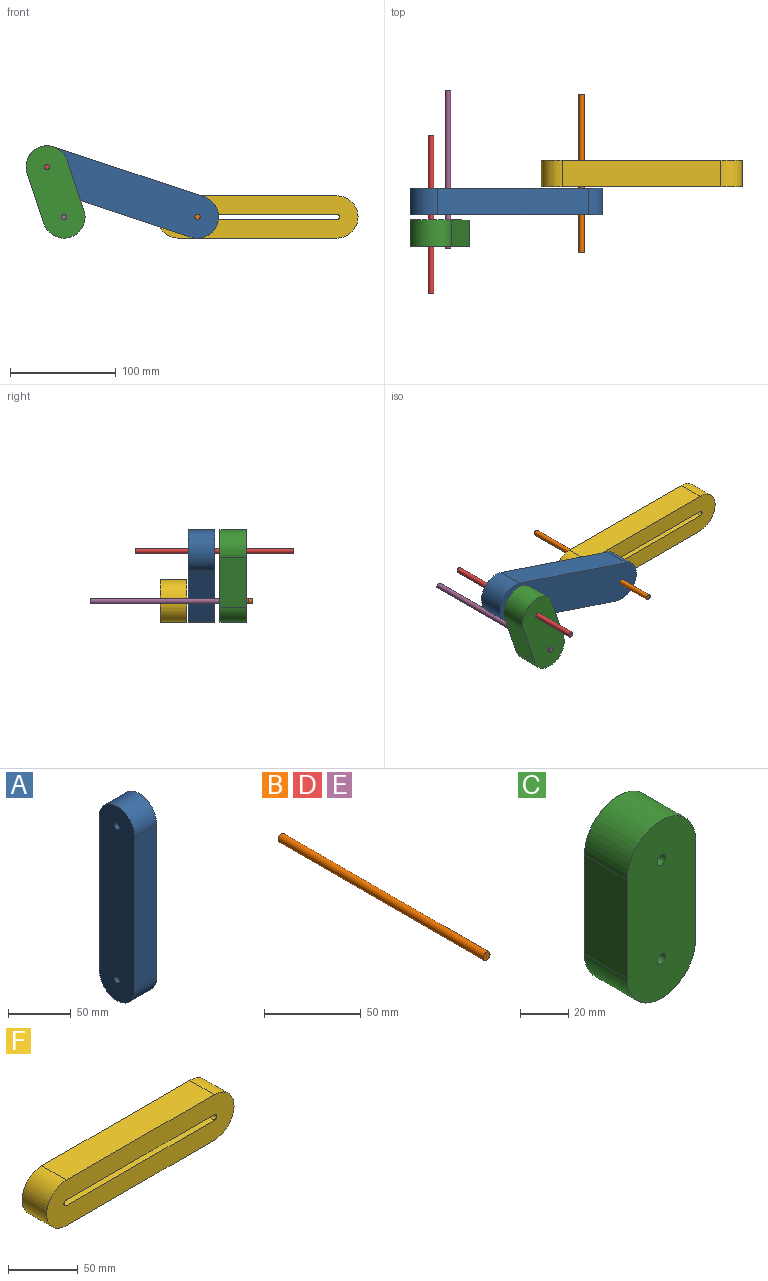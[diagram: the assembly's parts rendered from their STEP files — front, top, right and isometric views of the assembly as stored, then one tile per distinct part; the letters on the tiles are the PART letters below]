
ASSEMBLY  parts=6 mates=5
PART A: 8 faces, bbox 25x40x190 mm
  f0: plane 150x25mm, normal (0,-1,0), area 3750mm2, adj f1,f4,f6,f7
  f1: cylinder r=20mm len=40mm, axis (-1,0,0), area 1570.8mm2, adj f0,f2,f6,f7
  f2: plane 150x25mm, normal (0,1,0), area 3750mm2, adj f1,f4,f6,f7
  f3: cylinder r=2.5mm len=25mm, axis (-1,0,0), area 392.7mm2, adj f6,f7
  f4: cylinder r=20mm len=40mm, axis (-1,0,0), area 1570.8mm2, adj f0,f2,f6,f7
  f5: cylinder r=2.5mm len=25mm, axis (-1,0,0), area 392.7mm2, adj f6,f7
  f6: plane 190x40mm, normal (1,0,0), area 7217.4mm2, adj f0,f1,f2,f3,f4,f5
  f7: plane 190x40mm, normal (-1,0,0), area 7217.4mm2, adj f0,f1,f2,f3,f4,f5
PART B: 3 faces, bbox 5x150x5 mm
  f0: cylinder r=2.5mm len=150mm, axis (0,1,0), area 2356.2mm2, adj f1,f2
  f1: plane 5x5mm, normal (0,-1,0), area 19.6mm2, adj f0
  f2: plane 5x5mm, normal (0,1,0), area 19.6mm2, adj f0
PART C: 8 faces, bbox 40x25x90 mm
  f0: plane 50x25mm, normal (1,0,0), area 1250mm2, adj f1,f4,f6,f7
  f1: cylinder r=20mm len=40mm, axis (0,1,0), area 1570.8mm2, adj f0,f2,f6,f7
  f2: plane 50x25mm, normal (-1,0,0), area 1250mm2, adj f1,f4,f6,f7
  f3: cylinder r=2.5mm len=25mm, axis (0,1,0), area 392.7mm2, adj f6,f7
  f4: cylinder r=20mm len=40mm, axis (0,1,0), area 1570.8mm2, adj f0,f2,f6,f7
  f5: cylinder r=2.5mm len=25mm, axis (0,1,0), area 392.7mm2, adj f6,f7
  f6: plane 90x40mm, normal (0,-1,0), area 3217.4mm2, adj f0,f1,f2,f3,f4,f5
  f7: plane 90x40mm, normal (0,1,0), area 3217.4mm2, adj f0,f1,f2,f3,f4,f5
PART D: same geometry as B
PART E: same geometry as B
PART F: 10 faces, bbox 190x25x40 mm
  f0: plane 150x25mm, normal (0,0,-1), area 3750mm2, adj f1,f7,f8,f9
  f1: cylinder r=2.5mm len=25mm, axis (0,1,0), area 196.3mm2, adj f0,f2,f8,f9
  f2: plane 150x25mm, normal (0,0,1), area 3750mm2, adj f1,f7,f8,f9
  f3: plane 150x25mm, normal (0,0,1), area 3750mm2, adj f4,f6,f8,f9
  f4: cylinder r=20mm len=40mm, axis (0,1,0), area 1570.8mm2, adj f3,f5,f8,f9
  f5: plane 150x25mm, normal (0,0,-1), area 3750mm2, adj f4,f6,f8,f9
  f6: cylinder r=20mm len=40mm, axis (0,1,0), area 1570.8mm2, adj f3,f5,f8,f9
  f7: cylinder r=2.5mm len=25mm, axis (0,1,0), area 196.3mm2, adj f0,f2,f8,f9
  f8: plane 190x40mm, normal (0,-1,0), area 6487mm2, adj f0,f1,f2,f3,f4,f5,f6,f7
  f9: plane 190x40mm, normal (0,1,0), area 6487mm2, adj f0,f1,f2,f3,f4,f5,f6,f7
PLACE A rot(axis=(0.63,0.63,0.45),131.1deg) t=(-48.24,-76.78,81.14)mm
PLACE B rot(axis=(0,1,0),98.2deg) t=(100.41,37.22,52.76)mm
PLACE C rot(axis=(0,-1,0),18.5deg) t=(-26.02,-81.78,52.71)mm
PLACE D rot(axis=(0,-1,0),90deg) t=(-41.92,-1.78,100.12)mm
PLACE E rot(axis=(0,1,0),89.9deg) t=(-26.02,41.22,52.71)mm fixed
PLACE F t=(82.32,-25.28,52.76)mm fixed
MATE cylindrical E.f0 <-> C.f4  axis (0,-1,0) through (-26.02,-108.78,52.71)mm
MATE cylindrical A.f4 <-> B.f0  axis (0,-1,0) through (100.41,-76.78,52.76)mm
MATE cylindrical D.f0 <-> A.f1  axis (0,1,0) through (-41.92,-1.78,100.12)mm
MATE cylindrical C.f1 <-> D.f0  axis (0,-1,0) through (-41.92,-106.78,100.12)mm
MATE pin_slot B.f0 <-> F.f7  axis (0,1,0) through (100.41,-37.78,52.76)mm
